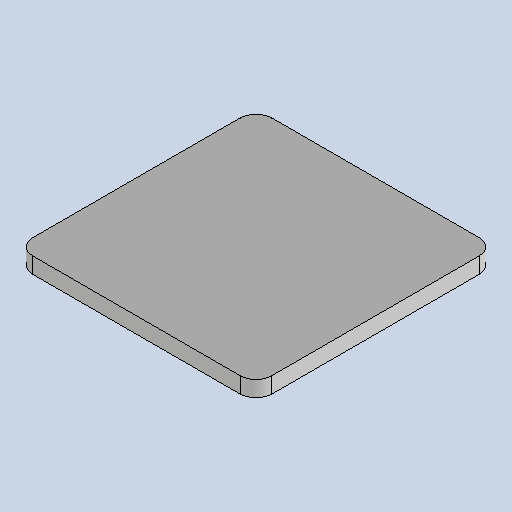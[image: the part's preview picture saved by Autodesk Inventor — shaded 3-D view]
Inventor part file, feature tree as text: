
AUTODESK INVENTOR PART (.ipt)
format: ipt  version: 2025.1 (Build 291241020, 241B)  size: 142,336 bytes
history: native  units: mm
features: other x2, sheet_metal_op x1, chamfer x1, sketch x1
ambient origin geometry x8: Origin, YZ Plane, XZ Plane, XY Plane, X Axis, Y Axis, Z Axis, Center Point
bodies: Body1 (feature_tree)
feature tree (5):
  sheet_metal_op  "Face3"
  chamfer  "Corner Round1"
  sketch  "Sketch1"  dims[d154=30.0mm d155=30.0mm d156=2.0mm d178=2.0mm]
  other  "Plate5"
  other  "Definition1"
